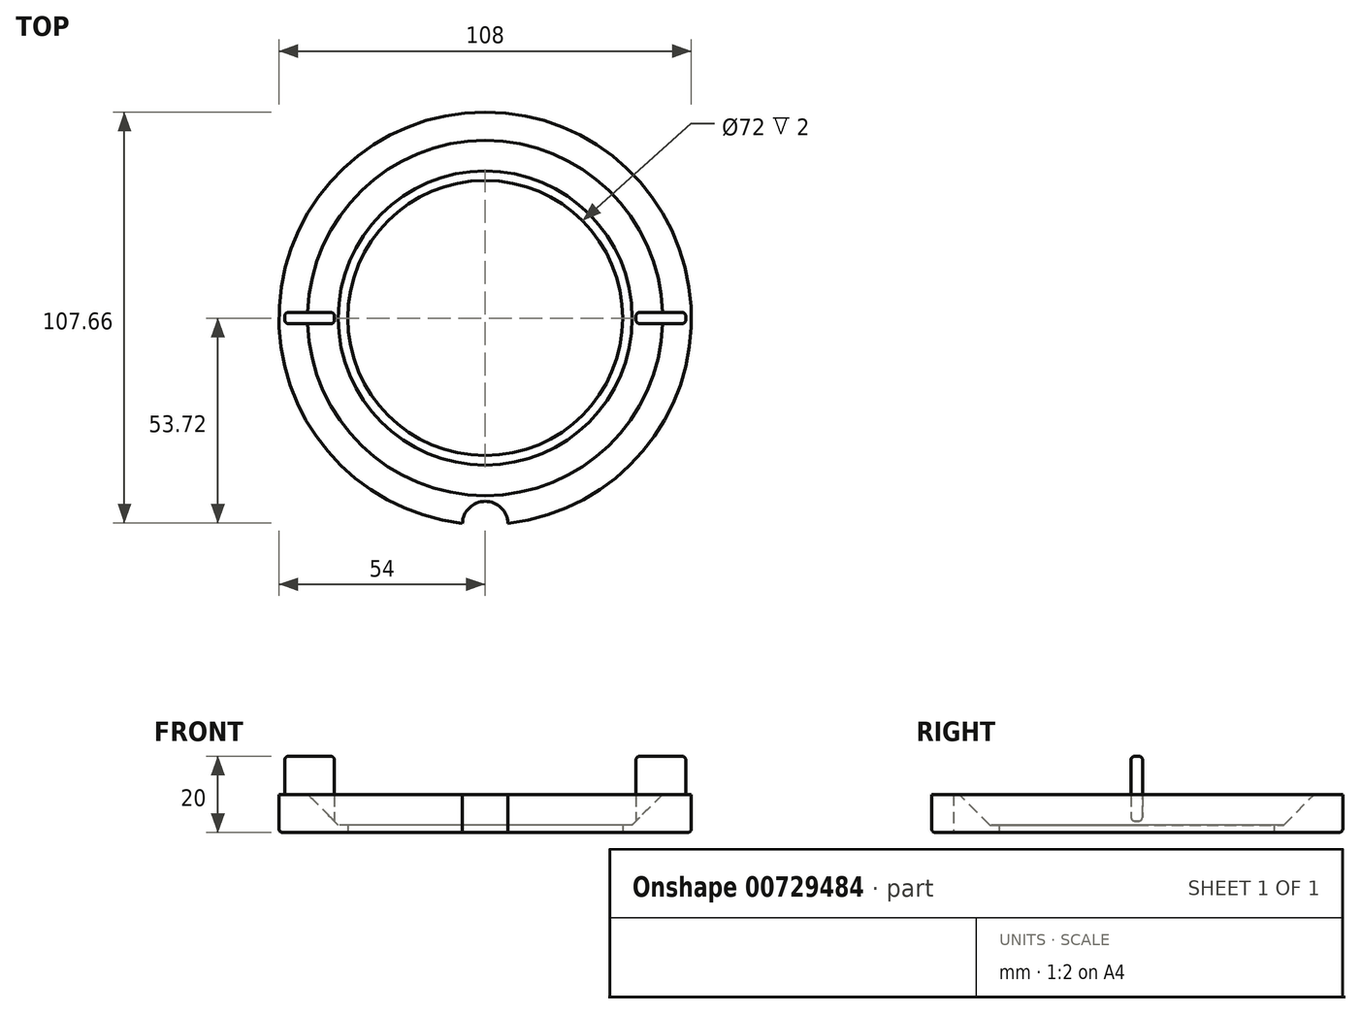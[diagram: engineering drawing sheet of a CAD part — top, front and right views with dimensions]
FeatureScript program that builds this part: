
annotation { "Feature Type Name" : "Feature", "Feature Type Description" : "" }
export const myFeature = defineFeature(function(context is Context, id is Id, definition is map)
    precondition{}
    {
        {
            var Q0;
            Q0=qCreatedBy(makeId("Top.planeOp"),FACE);
            var sketch = newSketch(context, id + "F0", { "sketchPlane" : qUnion([Q0])});
            skCircle(sketch, "E0", {"center": v(0, 0) * mm, "radius": 38.5 * mm});
            skCircle(sketch, "E1", {"center": v(0, 0) * mm, "radius": 36 * mm});
            skPoint(sketch, "E2", {"position": v(-46, 0) * mm});
            skPoint(sketch, "E3", {"position": v(46, 0) * mm});
            skLineSegment(sketch, "E4.bottom", {"start": v(-39.5, -1.5) * mm, "end": v(-52.5, -1.5) * mm});
            skLineSegment(sketch, "E4.top", {"start": v(-39.5, 1.5) * mm, "end": v(-52.5, 1.5) * mm});
            skLineSegment(sketch, "E4.left", {"start": v(-39.5, -1.5) * mm, "end": v(-39.5, 1.5) * mm});
            skLineSegment(sketch, "E4.right", {"start": v(-52.5, -1.5) * mm, "end": v(-52.5, 1.5) * mm});
            skLineSegment(sketch, "E5.bottom", {"start": v(52.5, -1.5) * mm, "end": v(39.5, -1.5) * mm});
            skLineSegment(sketch, "E5.top", {"start": v(52.5, 1.5) * mm, "end": v(39.5, 1.5) * mm});
            skLineSegment(sketch, "E5.left", {"start": v(52.5, -1.5) * mm, "end": v(52.5, 1.5) * mm});
            skLineSegment(sketch, "E5.right", {"start": v(39.5, -1.5) * mm, "end": v(39.5, 1.5) * mm});
            skArc(sketch, "E6", {"start": v(6, -53.72) * mm, "mid": v(0, -48) * mm, "end": v(-6, -53.72) * mm});
            skArc(sketch, "E7", {"start": v(6, -53.72) * mm, "mid": v(0, 53.94) * mm, "end": v(-6, -53.72) * mm});
            skSolve(sketch);
        }
        {
            var Q0;
            Q0=makeQuery(id+"F0.imprint","IMPRINT",FACE,{"disambiguationData":[TD([[makeQuery(id+"F0.imprint","IMPRINT",EDGE,{"derivedFrom":sQuery(id+"F0.wireOp",EDGE,"E0")}),-1.0]])]});
            extrude(context, id + "F1", {"entities" : qUnion([Q0]), "depth" : 10 * mm, "offsetDistance" : 25 * mm});
        }
        {
            var Q0;
            Q0=makeQuery(id+"F0.imprint","IMPRINT",FACE,{"disambiguationData":[TD([[makeQuery(id+"F0.imprint","IMPRINT",EDGE,{"derivedFrom":sQuery(id+"F0.wireOp",EDGE,"E4.bottom")}),-1.0]])]});
            var Q1;
            Q1=makeQuery(id+"F0.imprint","IMPRINT",FACE,{"disambiguationData":[TD([[makeQuery(id+"F0.imprint","IMPRINT",EDGE,{"derivedFrom":sQuery(id+"F0.wireOp",EDGE,"E5.bottom")}),-1.0]])]});
            extrude(context, id + "F2", {"entities" : qUnion([Q0, Q1]), "operationType" : NewBodyOperationType.ADD, "depth" : 20 * mm, "offsetDistance" : 25 * mm});
        }
        {
            var Q0;
            Q0=makeQuery(id+"F0.imprint","IMPRINT",FACE,{"disambiguationData":[TD([[makeQuery(id+"F0.imprint","IMPRINT",EDGE,{"derivedFrom":sQuery(id+"F0.wireOp",EDGE,"E0")}),1.0]])]});
            extrude(context, id + "F3", {"entities" : qUnion([Q0]), "operationType" : NewBodyOperationType.ADD, "depth" : 2 * mm, "offsetDistance" : 25 * mm});
        }
        {
            var Q0;
            Q0=makeQuery(id+"F1.opExtrude","CAP_EDGE",EDGE,{"disambiguationData":[OSD([sQuery(id+"F0.wireOp",EDGE,"E0")])],"isStart":false});
            chamfer(context, id + "F4", {"entities" : qUnion([Q0]), "width" : 8 * mm, "tangentPropagation" : true});
        }
        {
            var Q0;
            Q0=makeQuery(id+"F2.opExtrude","CAP_EDGE",EDGE,{"disambiguationData":[OSD([sQuery(id+"F0.wireOp",EDGE,"E4.bottom")])],"isStart":false});
            var Q1;
            Q1=makeQuery(id+"F2.opExtrude","CAP_EDGE",EDGE,{"disambiguationData":[OSD([sQuery(id+"F0.wireOp",EDGE,"E4.top")])],"isStart":false});
            var Q2;
            Q2=makeQuery(id+"F2.opExtrude","CAP_EDGE",EDGE,{"disambiguationData":[OSD([sQuery(id+"F0.wireOp",EDGE,"E4.right")])],"isStart":false});
            var Q3;
            Q3=makeQuery(id+"F2.opExtrude","CAP_EDGE",EDGE,{"disambiguationData":[OSD([sQuery(id+"F0.wireOp",EDGE,"E4.left")])],"isStart":false});
            var Q4;
            Q4=makeQuery(id+"F2.opExtrude","CAP_EDGE",EDGE,{"disambiguationData":[OSD([sQuery(id+"F0.wireOp",EDGE,"E5.left")])],"isStart":false});
            var Q5;
            Q5=makeQuery(id+"F2.opExtrude","CAP_EDGE",EDGE,{"disambiguationData":[OSD([sQuery(id+"F0.wireOp",EDGE,"E5.right")])],"isStart":false});
            var Q6;
            Q6=makeQuery(id+"F2.opExtrude","CAP_EDGE",EDGE,{"disambiguationData":[OSD([sQuery(id+"F0.wireOp",EDGE,"E5.top")])],"isStart":false});
            var Q7;
            Q7=makeQuery(id+"F2.opExtrude","CAP_EDGE",EDGE,{"disambiguationData":[OSD([sQuery(id+"F0.wireOp",EDGE,"E5.bottom")])],"isStart":false});
            var Q8;
            Q8=makeQuery(id+"F1.opExtrude","CAP_EDGE",EDGE,{"disambiguationData":[OSD([sQuery(id+"F0.wireOp",EDGE,"E7")])],"isStart":true});
            var Q9;
            Q9=makeQuery(id+"F2.opExtrude","SWEPT_EDGE",EDGE,{"disambiguationData":[OSD([sQuery(id+"F0.wireOp",EDGE,"E4.bottom"),sQuery(id+"F0.wireOp",EDGE,"E4.right")])]});
            var Q10;
            Q10=makeQuery(id+"F2.opExtrude","SWEPT_EDGE",EDGE,{"disambiguationData":[OSD([sQuery(id+"F0.wireOp",EDGE,"E4.top"),sQuery(id+"F0.wireOp",EDGE,"E4.right")])]});
            var Q11;
            Q11=makeQuery(id+"F2.opExtrude","SWEPT_EDGE",EDGE,{"disambiguationData":[OSD([sQuery(id+"F0.wireOp",EDGE,"E4.bottom"),sQuery(id+"F0.wireOp",EDGE,"E4.left")])]});
            var Q12;
            Q12=makeQuery(id+"F2.opExtrude","SWEPT_EDGE",EDGE,{"disambiguationData":[OSD([sQuery(id+"F0.wireOp",EDGE,"E4.top"),sQuery(id+"F0.wireOp",EDGE,"E4.left")])]});
            var Q13;
            Q13=makeQuery(id+"F2.opExtrude","SWEPT_EDGE",EDGE,{"disambiguationData":[OSD([sQuery(id+"F0.wireOp",EDGE,"E5.top"),sQuery(id+"F0.wireOp",EDGE,"E5.right")])]});
            var Q14;
            Q14=makeQuery(id+"F2.opExtrude","SWEPT_EDGE",EDGE,{"disambiguationData":[OSD([sQuery(id+"F0.wireOp",EDGE,"E5.bottom"),sQuery(id+"F0.wireOp",EDGE,"E5.right")])]});
            var Q15;
            Q15=makeQuery(id+"F2.opExtrude","SWEPT_EDGE",EDGE,{"disambiguationData":[OSD([sQuery(id+"F0.wireOp",EDGE,"E5.bottom"),sQuery(id+"F0.wireOp",EDGE,"E5.left")])]});
            var Q16;
            Q16=makeQuery(id+"F2.opExtrude","SWEPT_EDGE",EDGE,{"disambiguationData":[OSD([sQuery(id+"F0.wireOp",EDGE,"E5.top"),sQuery(id+"F0.wireOp",EDGE,"E5.left")])]});
            fillet(context, id + "F5", {"entities" : qUnion([Q0, Q1, Q2, Q3, Q4, Q5, Q6, Q7, Q8, Q9, Q10, Q11, Q12, Q13, Q14, Q15, Q16]), "radius" : 1 * mm, "tangentPropagation" : true, "allowEdgeOverflow" : false});
        }
    });
